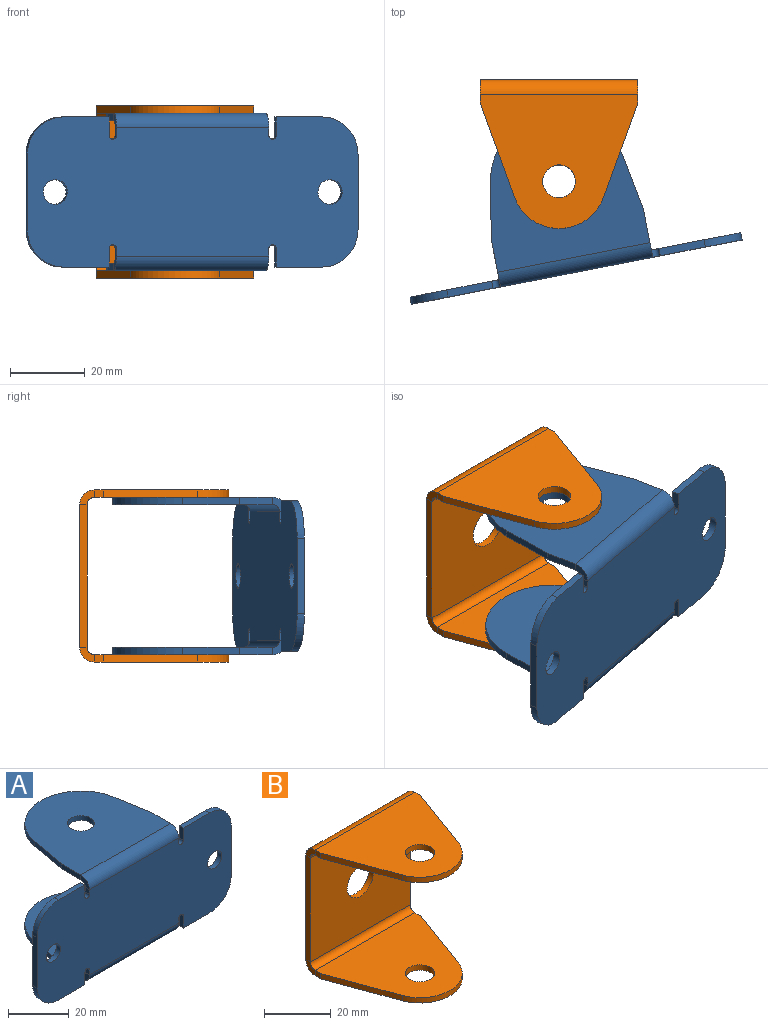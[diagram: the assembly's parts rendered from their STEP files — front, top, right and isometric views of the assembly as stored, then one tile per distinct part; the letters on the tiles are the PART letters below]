
ASSEMBLY  parts=2 mates=1
PART A: 50 faces, bbox 90.3x43.2x42.2 mm
  f0: plane 12.28x1.95mm, normal (0,0,1), area 23.9mm2, adj f2,f3,f11,f19
  f1: plane 12.28x1.95mm, normal (0,0,-1), area 23.9mm2, adj f2,f3,f9,f13
  f2: plane 90.25x40.25mm, normal (0,-1,0), area 3183.4mm2, adj f0,f1,f4,f5,f6,f7,f8,f9
  f3: plane 90.25x40.25mm, normal (0,1,0), area 3183.4mm2, adj f0,f1,f4,f5,f6,f7,f8,f9
  f4: plane 12.28x1.95mm, normal (0,0,-1), area 23.9mm2, adj f2,f3,f8,f15
  f5: plane 20.25x1.95mm, normal (1,0,0), area 39.5mm2, adj f2,f3,f8,f11
  f6: plane 12.28x1.95mm, normal (0,0,1), area 23.9mm2, adj f2,f3,f10,f21
  f7: plane 20.25x1.95mm, normal (-1,0,0), area 39.5mm2, adj f2,f3,f9,f10
  f8: cylinder r=10mm len=10mm, axis (0,-1,0), area 30.6mm2, adj f2,f3,f4,f5
  f9: cylinder r=10mm len=10mm, axis (0,1,0), area 30.6mm2, adj f1,f2,f3,f7
  f10: cylinder r=10mm len=10mm, axis (0,-1,0), area 30.6mm2, adj f2,f3,f6,f7
  f11: cylinder r=10mm len=10mm, axis (0,1,0), area 30.6mm2, adj f0,f2,f3,f5
  f12: cylinder r=1.04mm len=2.07mm, axis (0,1,0), area 6.3mm2, adj f2,f3,f13,f14
  f13: plane 4.94x1.95mm, normal (1,0,0), area 9.6mm2, adj f1,f2,f3,f12
  f14: plane 1.96x1.95mm, normal (-1,0,0), area 3.8mm2, adj f2,f3,f12,f32
  f15: plane 4.94x1.95mm, normal (-1,0,0), area 9.6mm2, adj f2,f3,f4,f16
  f16: cylinder r=1.04mm len=2.07mm, axis (0,1,0), area 6.3mm2, adj f2,f3,f15,f17
  f17: plane 1.96x1.95mm, normal (1,0,0), area 3.8mm2, adj f2,f3,f16,f31
  f18: cylinder r=1.04mm len=2.07mm, axis (0,1,0), area 6.3mm2, adj f2,f3,f19,f20
  f19: plane 4.94x1.95mm, normal (-1,0,0), area 9.6mm2, adj f0,f2,f3,f18
  f20: plane 1.96x1.95mm, normal (1,0,0), area 3.8mm2, adj f2,f3,f18,f42
  f21: plane 4.94x1.95mm, normal (1,0,0), area 9.6mm2, adj f2,f3,f6,f22
  f22: cylinder r=1.04mm len=2.07mm, axis (0,1,0), area 6.3mm2, adj f2,f3,f21,f23
  f23: plane 1.96x1.95mm, normal (-1,0,0), area 3.8mm2, adj f2,f3,f22,f43
  f24: plane 9x1.95mm, normal (1,0,0), area 17.6mm2, adj f28,f29,f30,f31
  f25: plane 9x1.95mm, normal (-1,0,0), area 17.6mm2, adj f26,f29,f30,f32
  f26: plane 15x2.64mm, normal (-0.98,0.17,0), area 29.7mm2, adj f25,f27,f29,f30
  f27: cylinder r=18.41mm len=36.26mm, axis (0,0,-1), area 100.3mm2, adj f26,f28,f29,f30
  f28: plane 15x2.64mm, normal (0.98,0.17,0), area 29.7mm2, adj f24,f27,f29,f30
  f29: plane 41.55x39.21mm, normal (0,0,-1), area 1311.9mm2, adj f24,f25,f26,f27,f28,f33,f47
  f30: plane 41.55x39.21mm, normal (0,0,1), area 1311.9mm2, adj f24,f25,f26,f27,f28,f34,f47
  f31: plane 3.95x3.95mm, normal (1,0,0), area 9.1mm2, adj f17,f24,f33,f34
  f32: plane 3.95x3.95mm, normal (-1,0,0), area 9.1mm2, adj f14,f25,f33,f34
  f33: cylinder r=3.95mm len=41.55mm, axis (1,0,0), area 257.8mm2, adj f2,f29,f31,f32
  f34: cylinder r=2mm len=41.55mm, axis (1,0,0), area 130.5mm2, adj f3,f30,f31,f32
  f35: plane 9x1.95mm, normal (-1,0,0), area 17.6mm2, adj f39,f40,f41,f43
  f36: plane 9x1.95mm, normal (1,0,0), area 17.6mm2, adj f37,f40,f41,f42
  f37: plane 15x2.64mm, normal (0.98,0.17,0), area 29.7mm2, adj f36,f38,f40,f41
  f38: cylinder r=18.41mm len=36.26mm, axis (0,0,1), area 100.3mm2, adj f37,f39,f40,f41
  f39: plane 15x2.64mm, normal (-0.98,0.17,0), area 29.7mm2, adj f35,f38,f40,f41
  f40: plane 41.55x39.21mm, normal (0,0,1), area 1311.9mm2, adj f35,f36,f37,f38,f39,f44,f46
  f41: plane 41.55x39.21mm, normal (0,0,-1), area 1311.9mm2, adj f35,f36,f37,f38,f39,f45,f46
  f42: plane 3.95x3.95mm, normal (1,0,0), area 9.1mm2, adj f20,f36,f44,f45
  f43: plane 3.95x3.95mm, normal (-1,0,0), area 9.1mm2, adj f23,f35,f44,f45
  f44: cylinder r=3.95mm len=41.55mm, axis (1,0,0), area 257.8mm2, adj f2,f40,f42,f43
  f45: cylinder r=2mm len=41.55mm, axis (1,0,0), area 130.5mm2, adj f3,f41,f42,f43
  f46: cylinder r=4.4mm len=8.8mm, axis (0,0,-1), area 53.9mm2, adj f40,f41
  f47: cylinder r=4.4mm len=8.8mm, axis (0,0,-1), area 53.9mm2, adj f29,f30
  f48: cylinder r=3.3mm len=6.6mm, axis (0,-1,0), area 40.4mm2, adj f2,f3
  f49: cylinder r=3.3mm len=6.6mm, axis (0,-1,0), area 40.4mm2, adj f2,f3
PART B: 29 faces, bbox 42.2x39.9x46.1 mm
  f0: plane 38.2x1.95mm, normal (1,0,0), area 74.5mm2, adj f2,f3,f12,f22
  f1: plane 38.2x1.95mm, normal (-1,0,0), area 74.5mm2, adj f2,f3,f11,f23
  f2: plane 42.2x38.2mm, normal (0,1,0), area 1517mm2, adj f0,f1,f13,f24,f28
  f3: plane 42.2x38.2mm, normal (0,-1,0), area 1517mm2, adj f0,f1,f14,f25,f28
  f4: plane 2.35x1.95mm, normal (-1,0,0), area 4.6mm2, adj f8,f9,f10,f11
  f5: plane 2.35x1.95mm, normal (1,0,0), area 4.6mm2, adj f6,f9,f10,f12
  f6: plane 25.28x9.2mm, normal (0.94,-0.34,0), area 52.5mm2, adj f5,f7,f9,f10
  f7: cylinder r=12.66mm len=23.8mm, axis (0,0,-1), area 60.3mm2, adj f6,f8,f9,f10
  f8: plane 25.28x9.2mm, normal (-0.94,-0.34,0), area 52.5mm2, adj f4,f7,f9,f10
  f9: plane 42.2x35.96mm, normal (0,0,-1), area 1016.9mm2, adj f4,f5,f6,f7,f8,f13,f27
  f10: plane 42.2x35.96mm, normal (0,0,1), area 1016.9mm2, adj f4,f5,f6,f7,f8,f14,f27
  f11: plane 3.95x3.95mm, normal (-1,0,0), area 9.1mm2, adj f1,f4,f13,f14
  f12: plane 3.95x3.95mm, normal (1,0,0), area 9.1mm2, adj f0,f5,f13,f14
  f13: cylinder r=3.95mm len=42.2mm, axis (-1,0,0), area 261.8mm2, adj f2,f9,f11,f12
  f14: cylinder r=2mm len=42.2mm, axis (-1,0,0), area 132.6mm2, adj f3,f10,f11,f12
  f15: plane 2.35x1.95mm, normal (1,0,0), area 4.6mm2, adj f19,f20,f21,f22
  f16: plane 2.35x1.95mm, normal (-1,0,0), area 4.6mm2, adj f17,f20,f21,f23
  f17: plane 25.28x9.2mm, normal (-0.94,-0.34,0), area 52.5mm2, adj f16,f18,f20,f21
  f18: cylinder r=12.66mm len=23.8mm, axis (0,0,1), area 60.3mm2, adj f17,f19,f20,f21
  f19: plane 25.28x9.2mm, normal (0.94,-0.34,0), area 52.5mm2, adj f15,f18,f20,f21
  f20: plane 42.2x35.96mm, normal (0,0,1), area 1016.9mm2, adj f15,f16,f17,f18,f19,f24,f26
  f21: plane 42.2x35.96mm, normal (0,0,-1), area 1016.9mm2, adj f15,f16,f17,f18,f19,f25,f26
  f22: plane 3.95x3.95mm, normal (1,0,0), area 9.1mm2, adj f0,f15,f24,f25
  f23: plane 3.95x3.95mm, normal (-1,0,0), area 9.1mm2, adj f1,f16,f24,f25
  f24: cylinder r=3.95mm len=42.2mm, axis (1,0,0), area 261.8mm2, adj f2,f20,f22,f23
  f25: cylinder r=2mm len=42.2mm, axis (1,0,0), area 132.6mm2, adj f3,f21,f22,f23
  f26: cylinder r=4.4mm len=8.8mm, axis (0,0,-1), area 53.9mm2, adj f20,f21
  f27: cylinder r=4.4mm len=8.8mm, axis (0,0,-1), area 53.9mm2, adj f9,f10
  f28: cylinder r=5.5mm len=11mm, axis (0,1,0), area 67.4mm2, adj f2,f3
PLACE A rot(axis=(0,0,1),11deg) t=(-5.68,1.95,0)mm
PLACE B at identity fixed
MATE revolute B.f7 <-> A.f38  axis (0,0,-1) through (0,-27.25,21.1)mm
